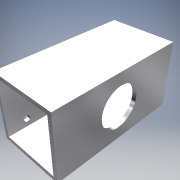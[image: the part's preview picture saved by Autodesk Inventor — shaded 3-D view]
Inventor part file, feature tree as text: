
AUTODESK INVENTOR PART (.ipt)
format: ipt  version: 2019 (Build 230136000, 136)  size: 142,848 bytes
history: native  units: in
note: dims shown in document units (in); Inventor stores cm internally (conversion verified against a paired STEP export)
features: reference x5, extrude x4, sketch x4, other x4
ambient origin geometry x8: Origin, YZ Plane, XZ Plane, XY Plane, X Axis, Y Axis, Z Axis, Center Point
bodies: Solid1 (feature_tree)
feature tree (17):
  extrude  "Extrusion1"  Depth=0.125in
  extrude  "Extrusion7"  Depth=2.0in
  extrude  "Extrusion8"  Depth=0.125in
  extrude  "Extrusion9"  Depth=1.0in TaperAngle=0.0deg
  sketch  "Sketch1"  dims[d0=2.0in d1=0.125in]
  sketch  "Sketch6"  dims[d2=4.0in d3=0.0in d11=2.0in]
  sketch  "Sketch7"  dims[d12=0.125in d23=1.125in]
  reference  "Reference2"
  reference  "Reference3"
  reference  "Reference4"
  reference  "Reference5"
  sketch  "Sketch8"  dims[d24=1.0in d25=0.0in d26=1.0in d27=0.0in d28=0.25in d29=0.437in d30=0.21in d31=1.0in d32=0.0in]
  reference  "Reference6"
  parser-record x1  (decoder bookkeeping rows leaked as tree rows — omitted from the tree; the rows remain in map.json)
  other  "Drive Arm.iam"
  other  "Arm 2 inch B:1"
  other  "Arm Bearing:1"
note: 1 file-system path scrubbed to <path> (originals preserved in map.json)
